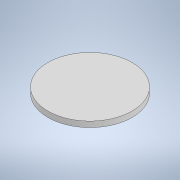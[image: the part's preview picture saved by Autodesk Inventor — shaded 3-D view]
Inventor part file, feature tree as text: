
AUTODESK INVENTOR PART (.ipt)
format: ipt  version: 2022.3 (Build 263350000, 350)  size: 91,136 bytes
history: native  units: in
note: dims shown in document units (in); Inventor stores cm internally (conversion verified against a paired STEP export)
features: extrude x1, sketch x1
ambient origin geometry x8: Origin, YZ Plane, XZ Plane, XY Plane, X Axis, Y Axis, Z Axis, Center Point
bodies: Solid1 (feature_tree)
feature tree (2):
  extrude  "Extrusion1"  Depth=0.1575in TaperAngle=0.0deg
  sketch  "Sketch1"  dims[d0=2.3622in d1=0.1575in d2=0.0in]
